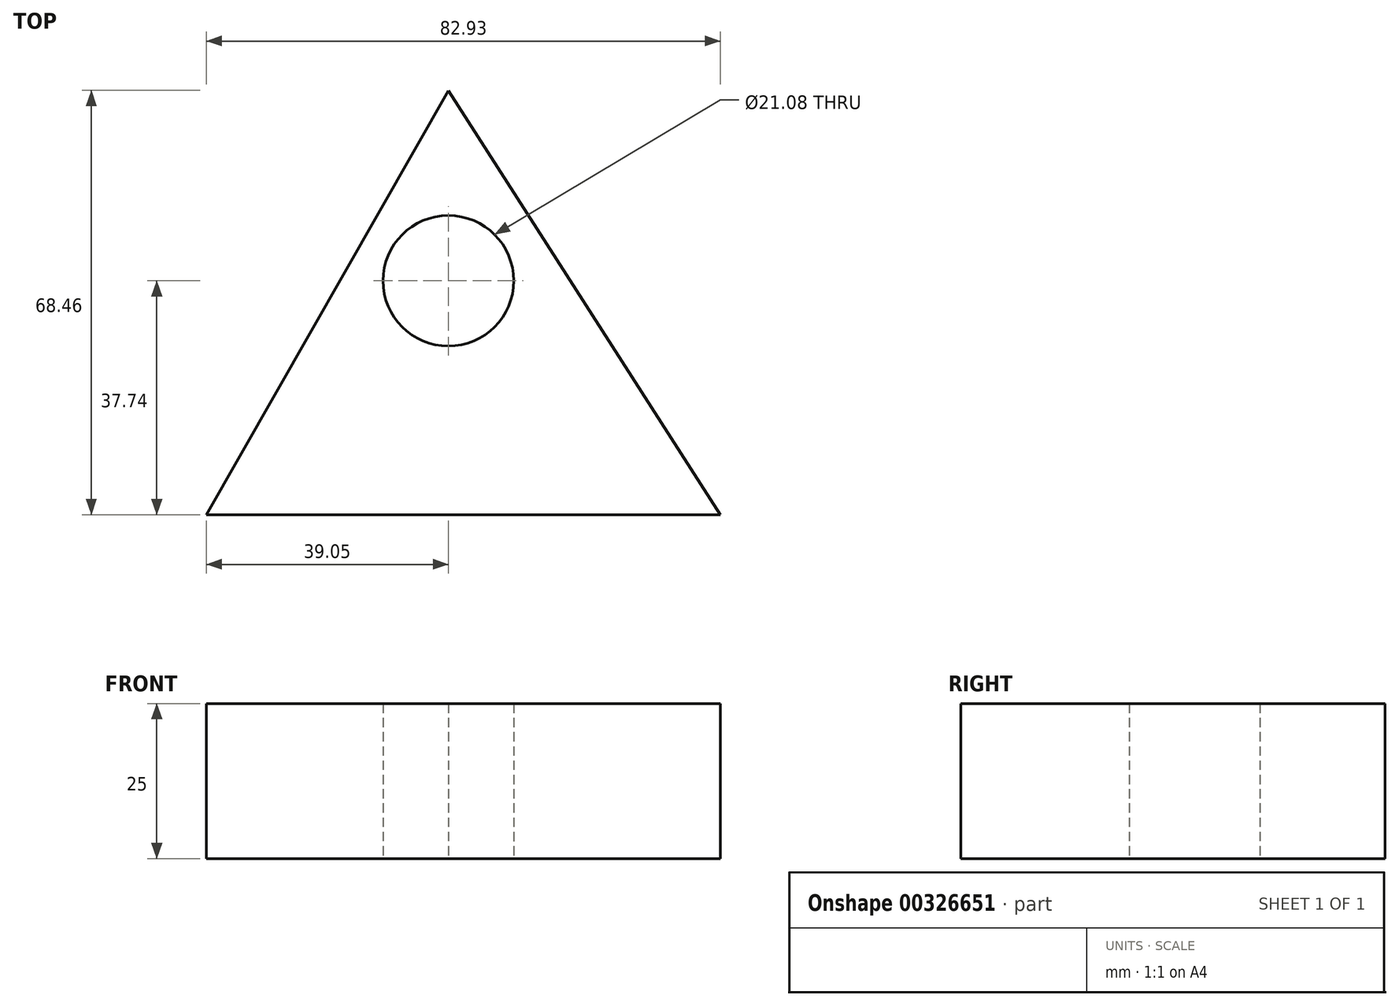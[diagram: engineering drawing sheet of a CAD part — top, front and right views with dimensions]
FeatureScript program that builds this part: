
annotation { "Feature Type Name" : "Feature", "Feature Type Description" : "" }
export const myFeature = defineFeature(function(context is Context, id is Id, definition is map)
    precondition{}
    {
        {
            var Q0;
            Q0=qCreatedBy(makeId("Top.planeOp"),FACE);
            var sketch = newSketch(context, id + "F0", { "sketchPlane" : qUnion([Q0])});
            skLineSegment(sketch, "E0", {"start": v(-39.05, -37.74) * mm, "end": v(43.88, -37.74) * mm});
            skLineSegment(sketch, "E1", {"start": v(43.88, -37.74) * mm, "end": v(0, 30.72) * mm});
            skLineSegment(sketch, "E2", {"start": v(0, 30.72) * mm, "end": v(-39.05, -37.74) * mm});
            skCircle(sketch, "E3", {"center": v(0, 0) * mm, "radius": 10.54 * mm});
            skSolve(sketch);
        }
        {
            var Q0;
            Q0=makeQuery(id+"F0.imprint","IMPRINT",FACE,{"disambiguationData":[TD([[makeQuery(id+"F0.imprint","IMPRINT",EDGE,{"derivedFrom":sQuery(id+"F0.wireOp",EDGE,"E0")}),1.0]])]});
            var sketch = newSketch(context, id + "F1", { "sketchPlane" : qUnion([Q0])});
            skSolve(sketch);
        }
        {
            var Q0;
            Q0 = qSketchRegion(id + "F1", true);
            var Q1;
            Q1=makeQuery(id+"F0.imprint","IMPRINT",FACE,{"disambiguationData":[TD([[makeQuery(id+"F0.imprint","IMPRINT",EDGE,{"derivedFrom":sQuery(id+"F0.wireOp",EDGE,"E0")}),1.0]])]});
            extrude(context, id + "F2", {"entities" : qUnion([Q0, Q1]), "depth" : 25 * mm});
        }
    });
